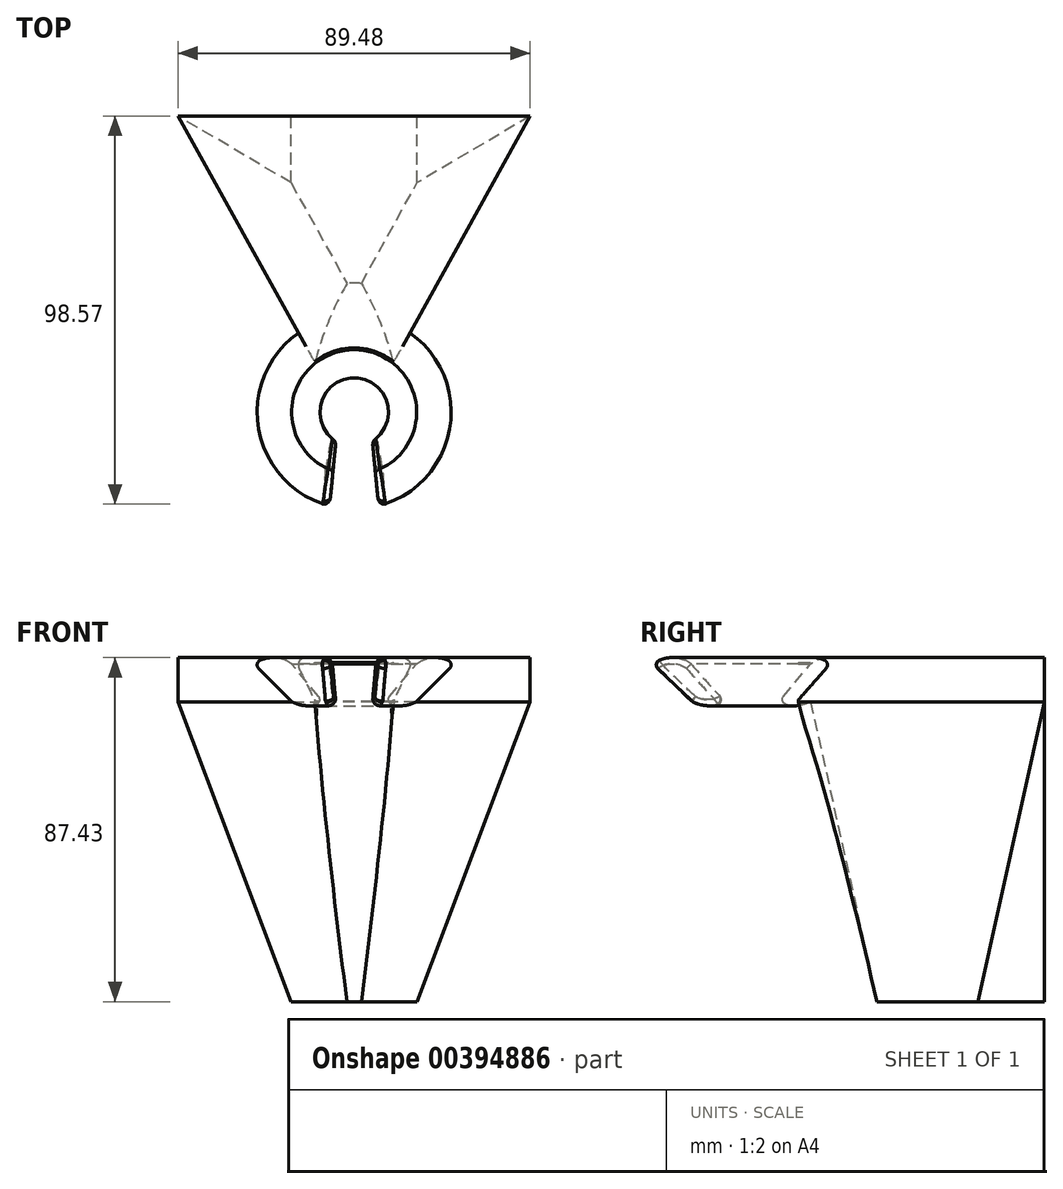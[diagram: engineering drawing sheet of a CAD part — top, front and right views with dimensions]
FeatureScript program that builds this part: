
annotation { "Feature Type Name" : "Feature", "Feature Type Description" : "" }
export const myFeature = defineFeature(function(context is Context, id is Id, definition is map)
    precondition{}
    {
        {
            var Q0;
            Q0=qCreatedBy(makeId("Top.planeOp"),FACE);
            cPlane(context, id + "F0", {"entities" : qUnion([Q0]), "cplaneType" : CPlaneType.OFFSET, "offset" : 9.52 * mm, "width" : 152.4 * mm, "height" : 152.4 * mm});
        }
        {
            var Q0;
            Q0=qCreatedBy(id+"F0.planeOp",FACE);
            var sketch = newSketch(context, id + "F1", { "sketchPlane" : qUnion([Q0])});
            skCircle(sketch, "E0.converted", {"center": v(0, 0) * mm, "radius": 15.88 * mm});
            skCircle(sketch, "E1.converted", {"center": v(0, 0) * mm, "radius": 25.4 * mm});
            skLineSegment(sketch, "E2", {"start": v(15.88, 0) * mm, "end": v(25.4, 0) * mm});
            skSolve(sketch);
        }
        {
            var Q0;
            Q0=qCreatedBy(makeId("Top.planeOp"),FACE);
            var sketch = newSketch(context, id + "F2", { "sketchPlane" : qUnion([Q0])});
            skCircle(sketch, "E3", {"center": v(0, 0) * mm, "radius": 15.88 * mm});
            skCircle(sketch, "E4", {"center": v(0, 0) * mm, "radius": 7.94 * mm});
            skLineSegment(sketch, "E5.0", {"start": v(15.88, 0) * mm, "end": v(25.4, 0) * mm, "construction": true});
            skPoint(sketch, "E5.1", {"position": v(20.64, 0) * mm});
            skLineSegment(sketch, "E6", {"start": v(15.88, 0) * mm, "end": v(7.94, 0) * mm});
            skSolve(sketch);
        }
        {
            var Q0;
            Q0=qCreatedBy(makeId("Front.planeOp"),FACE);
            var sketch = newSketch(context, id + "F3", { "sketchPlane" : qUnion([Q0])});
            skLineSegment(sketch, "E7.0", {"start": v(15.88, 0) * mm, "end": v(7.94, 0) * mm, "construction": true});
            skLineSegment(sketch, "E8.0", {"start": v(15.88, 9.53) * mm, "end": v(25.4, 9.53) * mm, "construction": true});
            skLineSegment(sketch, "E9", {"start": v(9, 1.27) * mm, "end": v(15.88, 9.53) * mm});
            skLineSegment(sketch, "E10", {"start": v(15.88, 0) * mm, "end": v(24.27, 8.4) * mm});
            skLineSegment(sketch, "E11", {"start": v(0, 0) * mm, "end": v(0, 11.14) * mm, "construction": true});
            skArc(sketch, "E12", {"start": v(23.9, 10.43) * mm, "mid": v(19.76, 11.1) * mm, "end": v(15.88, 9.53) * mm});
            skArc(sketch, "E13", {"start": v(9.6, -0.74) * mm, "mid": v(12.81, -1.04) * mm, "end": v(15.88, 0) * mm});
            skPoint(sketch, "E14.visualSharp", {"position": v(25.4, 9.53) * mm});
            skArc(sketch, "E14.filletArc", {"start": v(24.27, 8.4) * mm, "mid": v(24.62, 9.5) * mm, "end": v(23.9, 10.43) * mm});
            skPoint(sketch, "E15.visualSharp", {"position": v(7.94, 0) * mm});
            skArc(sketch, "E15.filletArc", {"start": v(9, 1.27) * mm, "mid": v(8.76, 0.1) * mm, "end": v(9.6, -0.74) * mm});
            skSolve(sketch);
        }
        {
            var Q0;
            Q0 = qSketchRegion(id + "F3", true);
            var Q1;
            Q1=sQuery(id+"F3.wireOp",EDGE,"E11");
            revolve(context, id + "F4", {"entities" : qUnion([Q0]), "axis" : qUnion([Q1]), "revolveType" : RevolveType.FULL});
        }
        {
            var Q0;
            Q0=qCreatedBy(id+"F0.planeOp",FACE);
            var sketch = newSketch(context, id + "F5", { "sketchPlane" : qUnion([Q0])});
            skLineSegment(sketch, "E16", {"start": v(0, -7.94) * mm, "end": v(0, -25.4) * mm, "construction": true});
            skCircle(sketch, "E17", {"center": v(0, -25.4) * mm, "radius": 6.35 * mm, "construction": true});
            skCircle(sketch, "E18", {"center": v(0, -7.94) * mm, "radius": 4.76 * mm, "construction": true});
            skLineSegment(sketch, "E19", {"start": v(-4.54, -6.5) * mm, "end": v(-6.3, -24.6) * mm});
            skLineSegment(sketch, "E20", {"start": v(4.54, -6.5) * mm, "end": v(6.3, -24.6) * mm});
            skArc(sketch, "E21.0", {"start": v(-4.54, -6.5) * mm, "mid": v(0, -7.94) * mm, "end": v(4.54, -6.5) * mm});
            skArc(sketch, "E22.0", {"start": v(-6.3, -24.6) * mm, "mid": v(0, -25.4) * mm, "end": v(6.3, -24.6) * mm});
            skSolve(sketch);
        }
        {
            var Q0;
            Q0 = qSketchRegion(id + "F5", true);
            extrude(context, id + "F6", {"entities" : qUnion([Q0]), "operationType" : NewBodyOperationType.REMOVE, "endBound" : BoundingType.SYMMETRIC, "oppositeDirection" : true, "depth" : 25.4 * mm});
        }
        {
            var Q0;
            Q0=makeQuery(id+"F6.boolean.opBoolean","COPY",FACE,{"derivedFrom":makeQuery(id+"F6.opExtrude","SWEPT_FACE",FACE,{"disambiguationData":[OSD([sQuery(id+"F5.wireOp",EDGE,"E19")])]})});
            var Q1;
            Q1=makeQuery(id+"F4.opRevolve","SWEPT_FACE",FACE,{"disambiguationData":[OSD([sQuery(id+"F3.wireOp",EDGE,"E10")])]});
            var Q2;
            Q2=makeQuery(id+"F6.boolean.opBoolean","COPY",FACE,{"derivedFrom":makeQuery(id+"F6.opExtrude","SWEPT_FACE",FACE,{"disambiguationData":[OSD([sQuery(id+"F5.wireOp",EDGE,"E20")])]})});
            fillet(context, id + "F7", {"entities" : qUnion([Q0, Q1, Q2]), "radius" : 1.59 * mm, "allowEdgeOverflow" : false});
        }
        {
            var Q0;
            Q0=qCreatedBy(makeId("Top.planeOp"),FACE);
            cPlane(context, id + "F8", {"entities" : qUnion([Q0]), "cplaneType" : CPlaneType.OFFSET, "offset" : 1.1 * mm, "oppositeDirection" : true, "width" : 152.4 * mm, "height" : 152.4 * mm});
        }
        {
            var Q0;
            Q0=qCreatedBy(id+"F8.planeOp",FACE);
            cPlane(context, id + "F9", {"entities" : qUnion([Q0]), "cplaneType" : CPlaneType.OFFSET, "offset" : 1.02 * mm, "width" : 152.4 * mm, "height" : 152.4 * mm});
        }
        {
            var Q0;
            Q0=qCreatedBy(id+"F9.planeOp",FACE);
            var sketch = newSketch(context, id + "F10", { "sketchPlane" : qUnion([Q0])});
            skLineSegment(sketch, "E23.0", {"start": v(44.74, 75.22) * mm, "end": v(10.1, 12.82) * mm});
            skLineSegment(sketch, "E24.0", {"start": v(44.74, 75.22) * mm, "end": v(-44.74, 75.22) * mm});
            skLineSegment(sketch, "E25.0", {"start": v(-44.74, 75.22) * mm, "end": v(-10.1, 12.82) * mm});
            skArc(sketch, "E26.0", {"start": v(9.36, 12.82) * mm, "mid": v(0, 15.88) * mm, "end": v(-9.36, 12.82) * mm});
            skLineSegment(sketch, "E27.0", {"start": v(9.36, 12.82) * mm, "end": v(10.1, 12.82) * mm});
            skLineSegment(sketch, "E28.0", {"start": v(-10.1, 12.82) * mm, "end": v(-9.36, 12.82) * mm});
            skSolve(sketch);
        }
        {
            var Q0;
            Q0 = qSketchRegion(id + "F10", true);
            extrude(context, id + "F11", {"entities" : qUnion([Q0]), "operationType" : NewBodyOperationType.ADD, "depth" : 11.23 * mm, "offsetDistance" : 25.4 * mm});
        }
        {
            var Q0;
            Q0=qCreatedBy(makeId("Top.planeOp"),FACE);
            cPlane(context, id + "F12", {"entities" : qUnion([Q0]), "cplaneType" : CPlaneType.OFFSET, "offset" : 88.9 * mm, "oppositeDirection" : true, "width" : 152.4 * mm, "height" : 152.4 * mm});
        }
        {
            var Q0;
            Q0=makeQuery(id+"F10.imprint","IMPRINT",FACE,{"disambiguationData":[TD([[makeQuery(id+"F10.imprint","IMPRINT",EDGE,{"derivedFrom":sQuery(id+"F10.wireOp",EDGE,"E23.0")}),-1.0]])]});
            extrude(context, id + "F13", {"entities" : qUnion([Q0]), "operationType" : NewBodyOperationType.ADD, "oppositeDirection" : true, "depth" : 76.2 * mm, "hasDraft" : true, "draftAngle" : 12.5 * degree, "draftPullDirection" : true, "offsetDistance" : 25.4 * mm});
        }
        {
            var Q0;
            {var subQ0=sQuery(id+"F10.wireOp",EDGE,"E28.0");var subQ1=sQuery(id+"F10.wireOp",EDGE,"E25.0");Q0=makeQuery(id+"F11.boolean.opBoolean","SPLIT",FACE,{"disambiguationData":[TD([makeQuery(id+"F4.opRevolve","SWEPT_FACE",FACE,{"disambiguationData":[OSD([sQuery(id+"F3.wireOp",EDGE,"E12")])]}),makeQuery(id+"F11.opExtrude","CAP_FACE",FACE,{"disambiguationData":[OSD([sQuery(id+"F10.wireOp",EDGE,"E23.0"),sQuery(id+"F10.wireOp",EDGE,"E24.0"),subQ1,sQuery(id+"F10.wireOp",EDGE,"E26.0"),sQuery(id+"F10.wireOp",EDGE,"E27.0"),subQ0])],"isStart":false}),makeQuery(id+"F11.opExtrude","SWEPT_FACE",FACE,{"disambiguationData":[OSD([subQ0])]})])],"derivedFrom":makeQuery(id+"F11.opExtrude","SWEPT_FACE",FACE,{"disambiguationData":[OSD([subQ1])]})});}
            var sketch = newSketch(context, id + "F14", { "sketchPlane" : qUnion([Q0])});
            skLineSegment(sketch, "E29.0", {"start": v(-20.4, 11.15) * mm, "end": v(-16.1, 11.15) * mm});
            skFitSpline(sketch, "E30.0", {"points": [v(-16.1, 9.84) * mm, v(-16.43, 10.05) * mm, v(-17.1, 10.42) * mm, v(-18.15, 10.83) * mm, v(-19.28, 11.09) * mm, v(-20.04, 11.15) * mm, v(-20.42, 11.15) * mm]});
            skLineSegment(sketch, "E31.0", {"start": v(-16.1, 11.15) * mm, "end": v(-15.75, 11.15) * mm});
            skLineSegment(sketch, "E32", {"start": v(-15.75, 11.15) * mm, "end": v(-15.37, 11.15) * mm});
            skLineSegment(sketch, "E33", {"start": v(-15.37, 11.15) * mm, "end": v(-15.37, 9.54) * mm});
            skLineSegment(sketch, "E34", {"start": v(-16.1, 9.84) * mm, "end": v(-15.36, 9.4) * mm});
            skLineSegment(sketch, "E35", {"start": v(-15.36, 9.4) * mm, "end": v(-15.37, 9.54) * mm});
            skSolve(sketch);
        }
        {
            var Q0;
            Q0=makeQuery(id+"F14.imprint","IMPRINT",FACE,{"disambiguationData":[TD([[makeQuery(id+"F14.imprint","IMPRINT",EDGE,{"derivedFrom":sQuery(id+"F14.wireOp",EDGE,"E29.0")}),-1.0]])]});
            var Q1;
            Q1=makeQuery(id+"F14.imprint","IMPRINT",FACE,{"disambiguationData":[TD([[makeQuery(id+"F14.imprint","IMPRINT",EDGE,{"derivedFrom":sQuery(id+"F14.wireOp",EDGE,"E31.0")}),-1.0]])]});
            var Q2;
            Q2=sQuery(id+"F3.wireOp",EDGE,"E11");
            revolve(context, id + "F15", {"operationType" : NewBodyOperationType.REMOVE, "entities" : qUnion([Q0, Q1]), "axis" : qUnion([Q2]), "revolveType" : RevolveType.ONE_DIRECTION, "oppositeDirection" : true, "angle" : 78.8 * degree});
        }
        {
            var Q0;
            Q0=makeQuery(id+"F11.opExtrude","SWEPT_FACE",FACE,{"disambiguationData":[OSD([sQuery(id+"F10.wireOp",EDGE,"E24.0")])]});
            var sketch = newSketch(context, id + "F16", { "sketchPlane" : qUnion([Q0])});
            skLineSegment(sketch, "E36.0", {"start": v(-16.04, -76.28) * mm, "end": v(16.04, -76.28) * mm});
            skLineSegment(sketch, "E37", {"start": v(-44.74, -0.08) * mm, "end": v(-16.04, -76.28) * mm});
            skLineSegment(sketch, "E38", {"start": v(16.04, -76.28) * mm, "end": v(44.74, -0.08) * mm});
            skLineSegment(sketch, "E39", {"start": v(44.74, -0.08) * mm, "end": v(-44.74, -0.08) * mm});
            skSolve(sketch);
        }
        {
            var Q0;
            Q0 = qSketchRegion(id + "F16", true);
            extrude(context, id + "F17", {"entities" : qUnion([Q0]), "operationType" : NewBodyOperationType.ADD, "endBound" : BoundingType.UP_TO_NEXT, "oppositeDirection" : true, "depth" : 25.4 * mm, "offsetDistance" : 25.4 * mm});
        }
    });
